# Revit family: Gleitschlitten Typ HV1, m.D., Ø219 - Ø457mm, (h=100-155 mm)
name_source: partatom
category: HLS-Bauteile
units: mm (PartAtom-declared; Revit-internal decimal feet)

## family parameters
Arbeitsebenenbasiert = Ja
Beim Laden mit Abzugskörper schneiden = Nein
Bemaßung runder Anschluss = Durchmesser verwenden
Beschriftungsausrichtung beibehalten = Nein
Gemeinsam genutzt = Ja
Immer vertikal = Nein
Klassifizierung = Keine
Raumberechnungspunkt = Nein
Teiletyp = Normal

## types (13) — shared parameters
Baustoffklasse = B2
Breite Schellenband = 50 mm
Dämmstärke = 6 mm  [stored 0.019685 ft]
Fabrikat = MEFA
Kurztext1 = Gleitschlitten A HV 100-155 50x5
Material = Stahl
Materialname = S235
Mengeneinheit = St
Schalldämmeinlage = Gummi EPDM
Sicherheitsfaktor = 1.54
Stärke Schellenband = 5 mm
Verschluss = Mutter / Verschluss-Schraube
Verschluss-Schraube = M12
Vorgabe-Ansicht = 1219 mm
max. Höhe Unterbau = 150 mm
max. Temperaturbeständigkeit = 100 °C
min. Höhe Unterbau = 100 mm
vpe = 1

## per-type parameters (varying)
| type | A (Breite) | Abstand Sperrscheibe | Achse Bohrloch | Artikelnummer | Breite Unterbau | EAN | Gewicht | Gewicht pro Bauteil | Kurztext2 | L | Länge Unterbau | Nennweite DN Rohr | Rohraußendurchmesser | Schellenteil | Stärke Material | TL-Fuß |
| Gleitschlitten HV1, m.D., Ø219mm, h=100mm bis h=155mm | 140 mm  [stored 0.459318 ft] | 14 mm  [stored 0.0459318 ft] | 90 mm  [stored 0.295276 ft] | 142afb0219 | 256 mm | 4250928462855 | 12.62 kg | 12.62 kg | 219 mm EPDM fsv | 270 mm  [stored 0.885827 ft] | 270 mm | 200 mm  [stored 0.656168 ft] | 219 mm  [stored 0.718504 ft] | Schellenteil für HV mit RS m.D : Schelleteil für 219 m.D. | 6 mm  [stored 0.019685 ft] | Gruppe Gleischlitten HV1 Ø219 bis 508 : Gl.0219 |
| Gleitschlitten HV1, m.D., Ø225mm, h=100mm bis h=155mm | 140 mm  [stored 0.459318 ft] | 14 mm  [stored 0.0459318 ft] | 90 mm  [stored 0.295276 ft] | 142afb0225 | 256 mm | 4250928462862 | 12.71 kg | 12.71 kg | 225 mm EPDM fsv | 270 mm  [stored 0.885827 ft] | 270 mm | 0 mm  [stored 0 ft] | 225 mm  [stored 0.738189 ft] | Schellenteil für HV mit RS m.D : Schelleteil für 225 m.D. | 6 mm  [stored 0.019685 ft] | Gruppe Gleischlitten HV1 Ø219 bis 508 : Gl.0225 |
| Gleitschlitten HV1, m.D., Ø273mm, h=100mm bis h=155mm | 172 mm  [stored 0.564304 ft] | 14 mm  [stored 0.0459318 ft] | 90 mm  [stored 0.295276 ft] | 142afb0273 | 288 mm | 4250928462879 | 13.79 kg | 13.79 kg | 273 mm EPDM fsv | 270 mm  [stored 0.885827 ft] | 270 mm | 250 mm  [stored 0.82021 ft] | 273 mm  [stored 0.895669 ft] | Schellenteil für HV mit RS m.D : Schelleteil für 273 m.D. | 6 mm  [stored 0.019685 ft] | Gruppe Gleischlitten HV1 Ø219 bis 508 : Gl.0273 |
| Gleitschlitten HV1, m.D., Ø280mm, h=100mm bis h=155mm | 172 mm  [stored 0.564304 ft] | 14 mm  [stored 0.0459318 ft] | 90 mm  [stored 0.295276 ft] | 142afb0280 | 288 mm | 4250928462886 | 13.91 kg | 13.91 kg | 280 mm EPDM fsv | 270 mm  [stored 0.885827 ft] | 270 mm | 0 mm  [stored 0 ft] | 280 mm  [stored 0.918635 ft] | Schellenteil für HV mit RS m.D : Schelleteil für 280 m.D. | 6 mm  [stored 0.019685 ft] | Gruppe Gleischlitten HV1 Ø219 bis 508 : Gl.0280 |
| Gleitschlitten HV1, m.D., Ø315mm, h=100mm bis h=155mm | 172 mm  [stored 0.564304 ft] | 14 mm  [stored 0.0459318 ft] | 90 mm  [stored 0.295276 ft] | 142afb0315 | 288 mm | 4250928462893 | 14.32 kg | 14.32 kg | 315 mm EPDM fsv | 270 mm  [stored 0.885827 ft] | 270 mm | 0 mm  [stored 0 ft] | 315 mm  [stored 1.03346 ft] | Schellenteil für HV mit RS m.D : Schelleteil für 315 m.D. | 6 mm  [stored 0.019685 ft] | Gruppe Gleischlitten HV1 Ø219 bis 508 : Gl.0315 |
| Gleitschlitten HV1, m.D., Ø324mm, h=100mm bis h=155mm | 172 mm  [stored 0.564304 ft] | 14 mm  [stored 0.0459318 ft] | 90 mm  [stored 0.295276 ft] | 142afb0324 | 288 mm | 4250928462909 | 14.47 kg | 14.47 kg | 324 mm EPDM fsv | 270 mm  [stored 0.885827 ft] | 270 mm | 300 mm | 324 mm  [stored 1.06299 ft] | Schellenteil für HV mit RS m.D : Schelleteil für 324 m.D. | 6 mm  [stored 0.019685 ft] | Gruppe Gleischlitten HV1 Ø219 bis 508 : Gl.0324 |
| Gleitschlitten HV1, m.D., Ø356mm, h=100mm bis h=155mm | 172 mm  [stored 0.564304 ft] | 14 mm  [stored 0.0459318 ft] | 90 mm  [stored 0.295276 ft] | 142afb0356 | 288 mm | 4250928462916 | 14.82 kg | 14.82 kg | 356 mm EPDM fsv | 270 mm  [stored 0.885827 ft] | 270 mm | 0 mm  [stored 0 ft] | 356 mm  [stored 1.16798 ft] | Schellenteil für HV mit RS m.D : Schelleteil für 356 m.D. | 6 mm  [stored 0.019685 ft] | Gruppe Gleischlitten HV1 Ø219 bis 508 : Gl.0356 |
| Gleitschlitten HV1, m.D., Ø400mm, h=100mm bis h=155mm | 225 mm  [stored 0.738189 ft] | 14 mm  [stored 0.0459318 ft] | 95 mm  [stored 0.31168 ft] | 142afb0400 | 341 mm | 4250928462923 | 18.64 kg | 18.64 kg | 400 mm EPDM fsv | 270 mm  [stored 0.885827 ft] | 270 mm | 0 mm  [stored 0 ft] | 400 mm  [stored 1.31234 ft] | Schellenteil für HV mit RS m.D : Schelleteil für 400 m.D. | 8 mm  [stored 0.0262467 ft] | Gruppe Gleischlitten HV1 Ø219 bis 508 : Gl.0400 |
| Gleitschlitten HV1, m.D., Ø406mm, h=100mm bis h=155mm | 225 mm  [stored 0.738189 ft] | 14 mm  [stored 0.0459318 ft] | 95 mm  [stored 0.31168 ft] | 142afb0406 | 341 mm | 4250928462930 | 18.80 kg | 18.80 kg | 406 mm EPDM fsv | 270 mm  [stored 0.885827 ft] | 270 mm | 400 mm  [stored 1.31234 ft] | 406 mm  [stored 1.33202 ft] | Schellenteil für HV mit RS m.D : Schelleteil für 406 m.D. | 8 mm  [stored 0.0262467 ft] | Gruppe Gleischlitten HV1 Ø219 bis 508 : Gl.0406 |
| Gleitschlitten HV1, m.D., Ø450mm, h=100mm bis h=155mm | 225 mm  [stored 0.738189 ft] | 14 mm  [stored 0.0459318 ft] | 95 mm  [stored 0.31168 ft] | 142afb0450 | 341 mm | 4250928462947 | 19.31 kg | 19.31 kg | 450 mm EPDM fsv | 270 mm  [stored 0.885827 ft] | 270 mm | 0 mm  [stored 0 ft] | 450 mm  [stored 1.47638 ft] | Schellenteil für HV mit RS m.D : Schelleteil für 450 m.D. | 8 mm  [stored 0.0262467 ft] | Gruppe Gleischlitten HV1 Ø219 bis 508 : Gl.0450 |
| Gleitschlitten HV1, m.D., Ø457mm, h=100mm bis h=155mm | 225 mm  [stored 0.738189 ft] | 14 mm  [stored 0.0459318 ft] | 95 mm  [stored 0.31168 ft] | 142afb0457 | 341 mm | 4250928462954 | 19.63 kg | 19.63 kg | 457 mm EPDM fsv | 270 mm  [stored 0.885827 ft] | 270 mm | 450 mm  [stored 1.47638 ft] | 457 mm  [stored 1.49934 ft] | Schellenteil für HV mit RS m.D : Schelleteil für 457 m.D. | 8 mm  [stored 0.0262467 ft] | Gruppe Gleischlitten HV1 Ø219 bis 508 : Gl.0457 |
| Gleitschlitten HV1, m.D., Ø500mm, h=100mm bis h=155mm | 254 mm  [stored 0.833333 ft] | 18 mm  [stored 0.0590551 ft] | 100 mm  [stored 0.328084 ft] | 142afb0500 | 370 mm | 4250928462961 | 25.77 kg | 25.77 kg | 500 mm EPDM fsv | 390 mm  [stored 1.27953 ft] | 390 mm | 0 mm  [stored 0 ft] | 500 mm  [stored 1.64042 ft] | Schellenteil für HV mit RS m.D : Schelleteil für 500 m.D. | 8 mm  [stored 0.0262467 ft] | Gruppe Gleischlitten HV1 Ø219 bis 508 : Gl.0500 |
| Gleitschlitten HV1, m.D., Ø508mm, h=100mm bis h=155mm | 254 mm  [stored 0.833333 ft] | 18 mm  [stored 0.0590551 ft] | 100 mm  [stored 0.328084 ft] | 142afb0508 | 370 mm | 4250928462978 | 25.89 kg | 25.89 kg | 508 mm EPDM fsv | 390 mm  [stored 1.27953 ft] | 390 mm | 500 mm  [stored 1.64042 ft] | 508 mm | Schellenteil für HV mit RS m.D : Schelleteil für 508 m.D. | 8 mm  [stored 0.0262467 ft] | Gruppe Gleischlitten HV1 Ø219 bis 508 : Gl.0508 |

note: [stored X ft] marks values corroborated as IEEE doubles in the binary element streams (Revit-internal decimal feet)

## geometry (parser evidence)
native form markers: Sweep x14
no freeform markers — native parametric forms only
